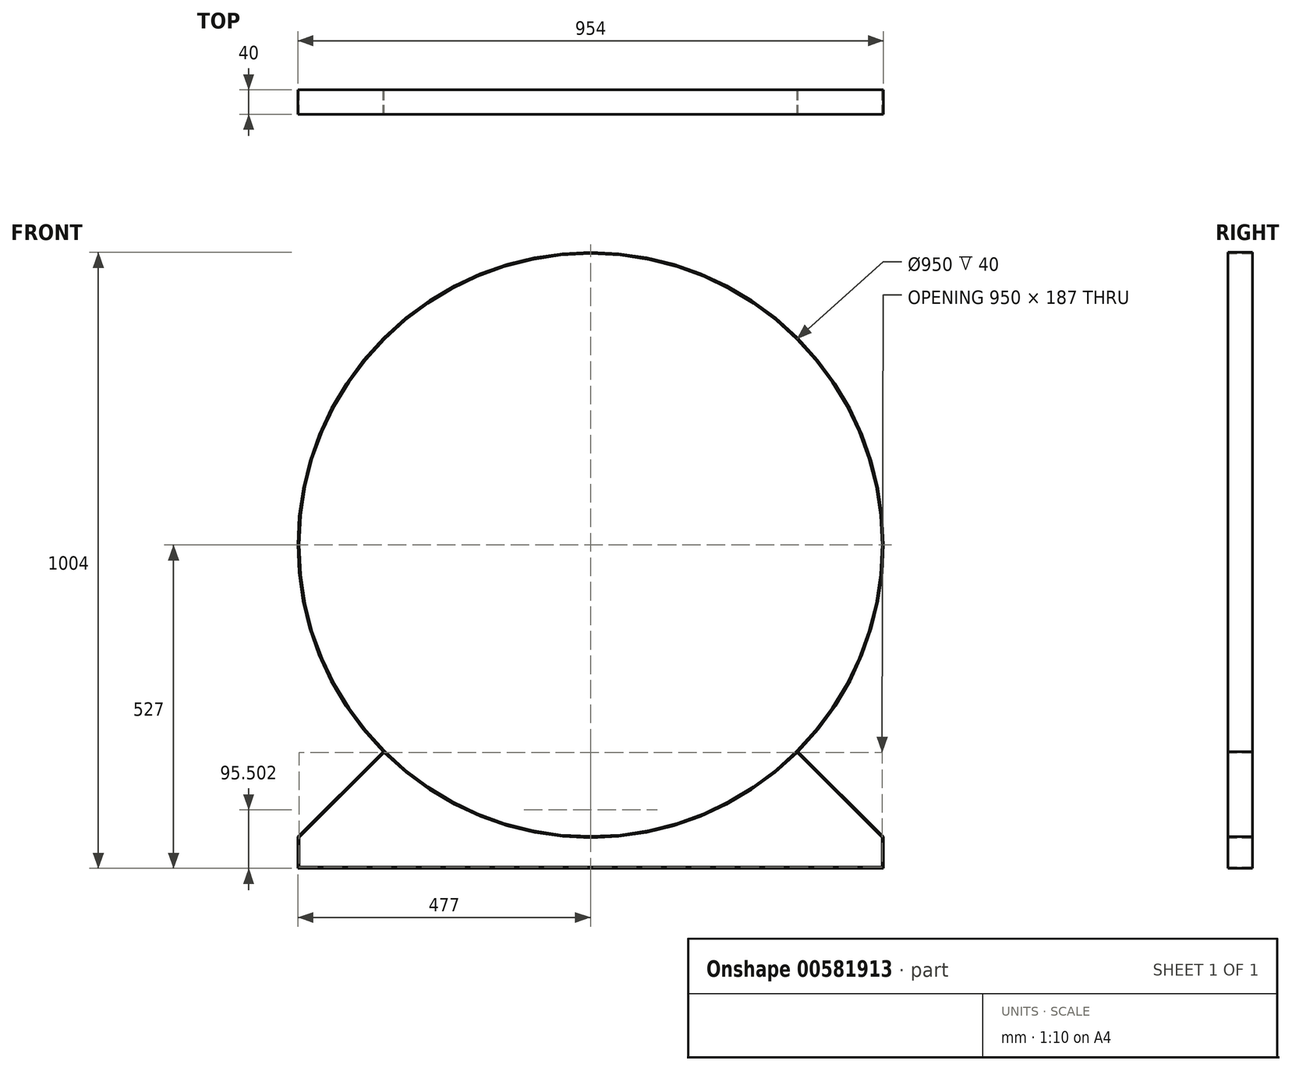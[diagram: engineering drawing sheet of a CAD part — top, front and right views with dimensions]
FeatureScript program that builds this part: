
annotation { "Feature Type Name" : "Feature", "Feature Type Description" : "" }
export const myFeature = defineFeature(function(context is Context, id is Id, definition is map)
    precondition{}
    {
        {
            var Q0;
            Q0=qCreatedBy(makeId("Front.planeOp"),FACE);
            var sketch = newSketch(context, id + "F0", { "sketchPlane" : qUnion([Q0])});
            skLineSegment(sketch, "E0", {"start": v(0, 0) * mm, "end": v(-679.96, 0) * mm, "construction": true});
            skLineSegment(sketch, "E1", {"start": v(0, 0) * mm, "end": v(0, 658.78) * mm, "construction": true});
            skLineSegment(sketch, "E2", {"start": v(0, 0) * mm, "end": v(-291.77, -291.77) * mm, "construction": true});
            skLineSegment(sketch, "E3", {"start": v(0, 0) * mm, "end": v(291.77, -291.77) * mm, "construction": true});
            skCircle(sketch, "E4", {"center": v(0, 0) * mm, "radius": 475 * mm});
            skCircle(sketch, "E5", {"center": v(0, 0) * mm, "radius": 477 * mm});
            skLineSegment(sketch, "E6", {"start": v(-477, -527) * mm, "end": v(0, -527) * mm});
            skLineSegment(sketch, "E7", {"start": v(-475, -525) * mm, "end": v(0, -525) * mm});
            skLineSegment(sketch, "E8", {"start": v(0, 0) * mm, "end": v(0, -311.11) * mm, "construction": true});
            skLineSegment(sketch, "E9", {"start": v(-475, -525) * mm, "end": v(-475, -476.41) * mm});
            skLineSegment(sketch, "E10", {"start": v(-477, -527) * mm, "end": v(-477, -475.59) * mm});
            skLineSegment(sketch, "E11", {"start": v(-338, -336.58) * mm, "end": v(-477, -475.59) * mm});
            skLineSegment(sketch, "E12", {"start": v(-336.58, -338) * mm, "end": v(-475, -476.41) * mm});
            skLineSegment(sketch, "E13.MirrorCS", {"start": v(336.58, -338) * mm, "end": v(475, -476.41) * mm});
            skLineSegment(sketch, "E14.MirrorCS", {"start": v(477, -527) * mm, "end": v(0, -527) * mm});
            skLineSegment(sketch, "E15.MirrorCS", {"start": v(475, -525) * mm, "end": v(0, -525) * mm});
            skLineSegment(sketch, "E16.MirrorCS", {"start": v(338, -336.58) * mm, "end": v(477, -475.59) * mm});
            skLineSegment(sketch, "E17.MirrorCS", {"start": v(475, -525) * mm, "end": v(475, -476.41) * mm});
            skLineSegment(sketch, "E18.MirrorCS", {"start": v(477, -527) * mm, "end": v(477, -475.59) * mm});
            skSolve(sketch);
        }
        {
            var Q0;
            Q0=qSketchRegion(id+"F0",true);
            extrude(context, id + "F1", {"entities" : qUnion([Q0]), "offsetDistance" : 25 * mm, "depth" : 40 * mm});
        }
    });
